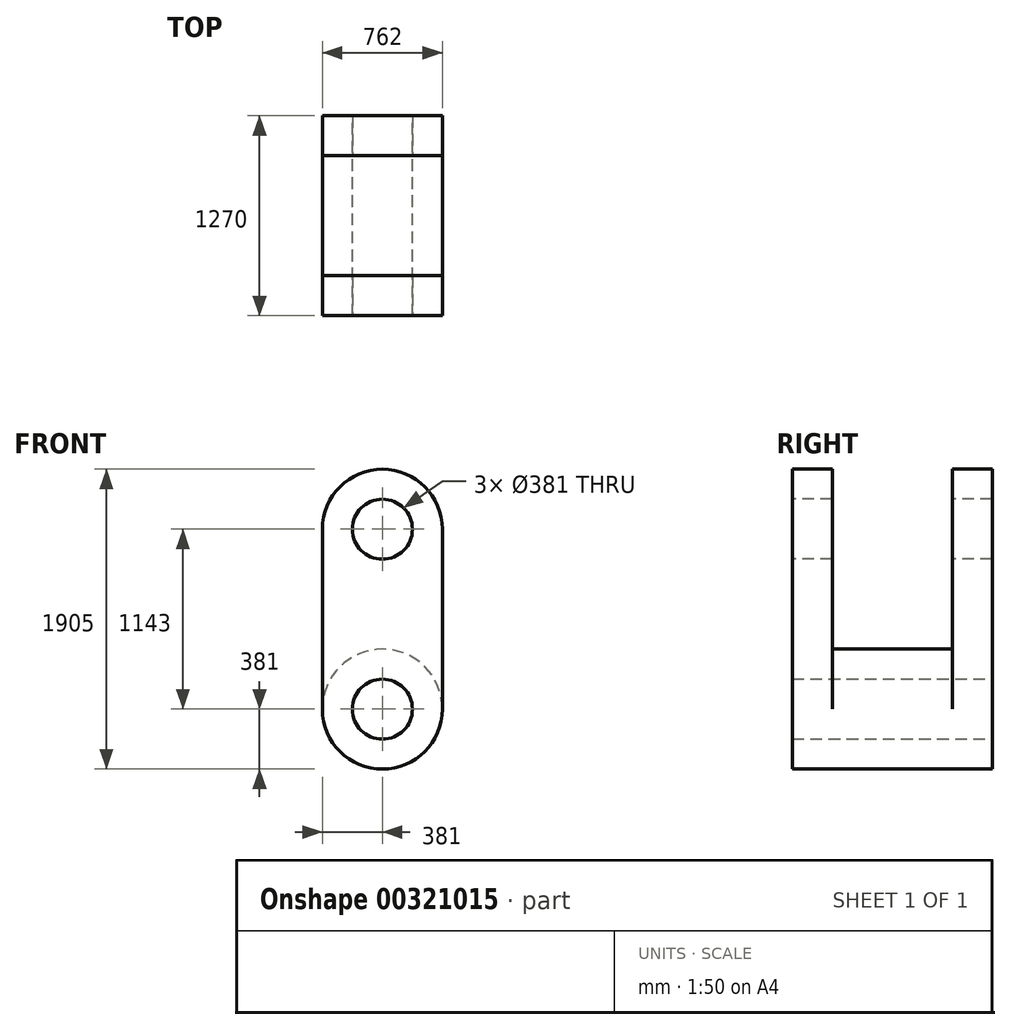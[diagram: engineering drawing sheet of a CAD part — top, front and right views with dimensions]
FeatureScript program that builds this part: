
annotation { "Feature Type Name" : "Feature", "Feature Type Description" : "" }
export const myFeature = defineFeature(function(context is Context, id is Id, definition is map)
    precondition{}
    {
        {
            var Q0;
            Q0=qCreatedBy(makeId("Front.planeOp"),FACE);
            var sketch = newSketch(context, id + "F0", { "sketchPlane" : qUnion([Q0])});
            skCircle(sketch, "E0", {"center": v(0, 0) * mm, "radius": 190.5 * mm});
            skCircle(sketch, "E1", {"center": v(0, 0) * mm, "radius": 381 * mm});
            skSolve(sketch);
        }
        {
            var Q0;
            Q0 = qSketchRegion(id + "F0", true);
            extrude(context, id + "F1", {"entities" : qUnion([Q0]), "depth" : 1016 * mm});
        }
        {
            var Q0;
            Q0=makeQuery(id+"F1.opExtrude","CAP_FACE",FACE,{"disambiguationData":[OSD([sQuery(id+"F0.wireOp",EDGE,"E0"),sQuery(id+"F0.wireOp",EDGE,"E1")])],"isStart":false});
            var sketch = newSketch(context, id + "F2", { "sketchPlane" : qUnion([Q0])});
            skArc(sketch, "E2", {"start": v(381, 1143) * mm, "mid": v(0, 1524) * mm, "end": v(-381, 1143) * mm});
            skCircle(sketch, "E3", {"center": v(0, 1143) * mm, "radius": 190.5 * mm});
            skLineSegment(sketch, "E4", {"start": v(-381, 1143) * mm, "end": v(-381, 0) * mm});
            skLineSegment(sketch, "E5", {"start": v(381, 1143) * mm, "end": v(381, 0) * mm});
            skArc(sketch, "E6.0", {"start": v(-381, 0) * mm, "mid": v(0, -381) * mm, "end": v(381, 0) * mm});
            skCircle(sketch, "E7.0", {"center": v(0, 0) * mm, "radius": 190.5 * mm});
            skSolve(sketch);
        }
        {
            var Q0;
            Q0 = qSketchRegion(id + "F2", true);
            extrude(context, id + "F3", {"entities" : qUnion([Q0]), "operationType" : NewBodyOperationType.ADD, "oppositeDirection" : true, "depth" : 254 * mm});
        }
        {
            var Q0;
            Q0=makeQuery(id+"F1.opExtrude","CAP_FACE",FACE,{"disambiguationData":[OSD([sQuery(id+"F0.wireOp",EDGE,"E0"),sQuery(id+"F0.wireOp",EDGE,"E1")])],"isStart":true});
            var sketch = newSketch(context, id + "F4", { "sketchPlane" : qUnion([Q0])});
            skLineSegment(sketch, "E8.0", {"start": v(-381, 1143) * mm, "end": v(-381, 0) * mm});
            skArc(sketch, "E9.0", {"start": v(-381, 1143) * mm, "mid": v(0, 1524) * mm, "end": v(381, 1143) * mm});
            skLineSegment(sketch, "E10.0", {"start": v(381, 1143) * mm, "end": v(381, 0) * mm});
            skArc(sketch, "E11.0", {"start": v(-381, 0) * mm, "mid": v(0, -381) * mm, "end": v(381, 0) * mm});
            skCircle(sketch, "E12.0", {"center": v(0, 0) * mm, "radius": 190.5 * mm});
            skCircle(sketch, "E13.0", {"center": v(0, 1143) * mm, "radius": 190.5 * mm});
            skSolve(sketch);
        }
        {
            var Q0;
            {var subQ1=sQuery(id+"F4.wireOp",EDGE,"E8.0");Q0=makeQuery(id+"F4.imprint","IMPRINT",FACE,{"disambiguationData":[TD([[makeQuery(id+"F4.imprint","IMPRINT",EDGE,{"derivedFrom":subQ1}),1.0]])]});}
            var Q1;
            {var subQ0=sQuery(id+"F4.wireOp",EDGE,"E11.0");Q1=makeQuery(id+"F4.imprint","IMPRINT",FACE,{"disambiguationData":[TD([[makeQuery(id+"F4.imprint","IMPRINT",EDGE,{"derivedFrom":subQ0}),-1.0]])]});}
            extrude(context, id + "F5", {"entities" : qUnion([Q0, Q1]), "operationType" : NewBodyOperationType.ADD, "depth" : 254 * mm});
        }
    });
